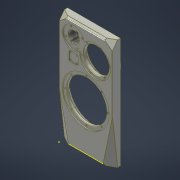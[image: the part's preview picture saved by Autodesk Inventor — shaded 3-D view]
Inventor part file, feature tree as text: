
AUTODESK INVENTOR PART (.ipt)
format: ipt  version: 2022 (Build 260153070, 153G)  size: 548,352 bytes
history: native  units: mm
features: other x24, sketch x15, chamfer x4, fillet x4, extrude x3, hole x3
ambient origin geometry x8: Origin, YZ Plane, XZ Plane, XY Plane, X Axis, Y Axis, Z Axis, Center Point
bodies: Body1 (feature_tree)
feature tree (53):
  other  "Аннотации"
  extrude  "Выдавливание2"  Depth=186.0mm
  hole  "Отверстие1"  [1 undecoded]
  extrude  "Выдавливание3"  Depth=102.0mm
  hole  "Отверстие3"  [1 undecoded]
  hole  "Отверстие4"  [1 undecoded]
  extrude  "Выдавливание4"  Depth=5.0mm
  sketch  "Эскиз9"
  sketch  "Эскиз10"
  other  "РабТочка1"
  other  "РабТочка2"
  other  "РабТочка3"
  other  "РабПлоскость1"
  other  "Разделение1"
  sketch  "Эскиз11"
  other  "РабТочка4"
  other  "РабТочка5"
  sketch  "Эскиз12"
  other  "РабТочка6"
  other  "РабПлоскость2"
  other  "Разделение2"
  sketch  "Эскиз13"
  sketch  "Эскиз14"
  sketch  "Эскиз15"
  other  "РабПлоскость3"
  other  "Разделение3"
  sketch  "Эскиз16"
  other  "РабПлоскость4"
  other  "Разделение4"
  chamfer  "Фаска1"  Distance=5.0mm
  chamfer  "Фаска2"  Distance=5.0mm
  chamfer  "Фаска3"  Distance=250.0mm
  chamfer  "Фаска4"  Distance=520.0mm
  fillet  "Сопряжение1"  Radius=120.0mm
  fillet  "Сопряжение2"  Radius=50.0mm
  fillet  "Сопряжение3"  Radius=40.0mm
  fillet  "Сопряжение4"  Radius=60.0mm
  sketch  "Эскиз17"
  sketch  "Эскиз1"
  sketch  "Эскиз3"
  sketch  "Эскиз4"
  sketch  "Эскиз6"
  sketch  "Эскиз7"
  sketch  "Эскиз8"
  other  "Линейный размер 1"
  other  "Линейный размер 2"
  other  "Линейный размер 3"
  other  "Линейный размер 4"
  other  "Линейный размер 5"
  other  "Линейный размер 6"
  other  "Линейный размер 7"
  other  "Линейный размер 8"
  other  "Линейный размер 9"
note: 3 required parameter values undecoded (feature->parameter linkage not recoverable at this tier; creation-order binding heuristic only, values carry confidence <= 0.55)
